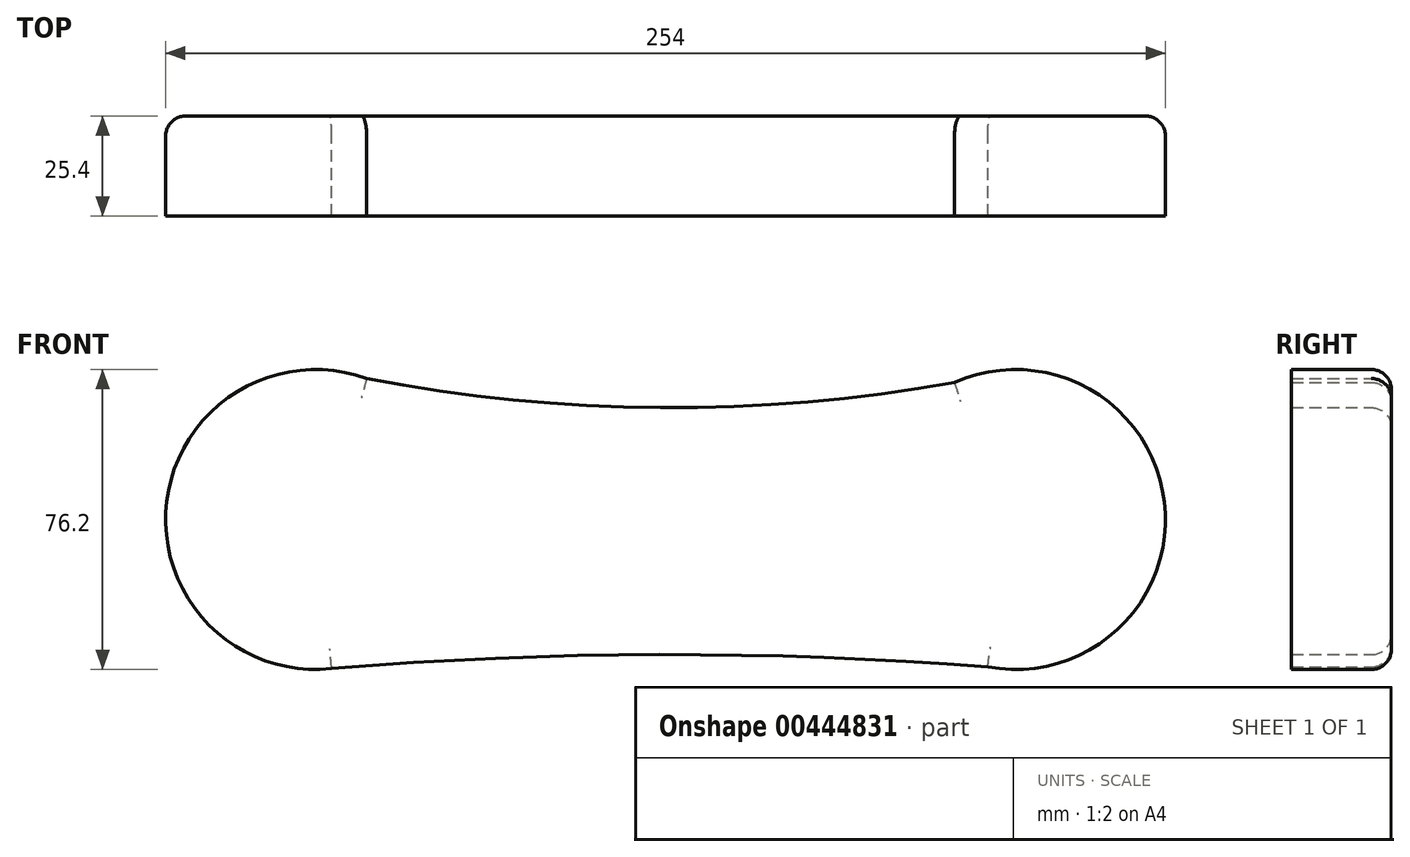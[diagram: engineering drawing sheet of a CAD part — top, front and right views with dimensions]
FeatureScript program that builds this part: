
annotation { "Feature Type Name" : "Feature", "Feature Type Description" : "" }
export const myFeature = defineFeature(function(context is Context, id is Id, definition is map)
    precondition{}
    {
        {
            var Q0;
            Q0=qCreatedBy(makeId("Front.planeOp"),FACE);
            var sketch = newSketch(context, id + "F0", { "sketchPlane" : qUnion([Q0])});
            skCircle(sketch, "E0", {"center": v(-88.67, 2.18) * mm, "radius": 38.1 * mm});
            skCircle(sketch, "E1", {"center": v(89.13, 2.18) * mm, "radius": 38.1 * mm});
            skArc(sketch, "E2", {"start": v(-86.4, 40.2) * mm, "mid": v(1.82, 30.6) * mm, "end": v(90.03, 40.26) * mm});
            skArc(sketch, "E3", {"start": v(90.03, -35.91) * mm, "mid": v(1.82, -32.15) * mm, "end": v(-86.4, -35.86) * mm});
            skSolve(sketch);
        }
        {
            var Q0;
            Q0 = qSketchRegion(id + "F0", true);
            extrude(context, id + "F1", {"entities" : qUnion([Q0]), "depth" : 25.4 * mm});
        }
        {
            var Q0;
            Q0=makeQuery(id+"F1.opExtrude","CAP_FACE",FACE,{"disambiguationData":[OSD([sQuery(id+"F0.wireOp",EDGE,"E0"),sQuery(id+"F0.wireOp",EDGE,"E1"),sQuery(id+"F0.wireOp",EDGE,"E2"),sQuery(id+"F0.wireOp",EDGE,"E3")])],"isStart":true});
            fillet(context, id + "F2", {"entities" : qUnion([Q0]), "radius" : 5.08 * mm, "tangentPropagation" : true, "allowEdgeOverflow" : false});
        }
    });
